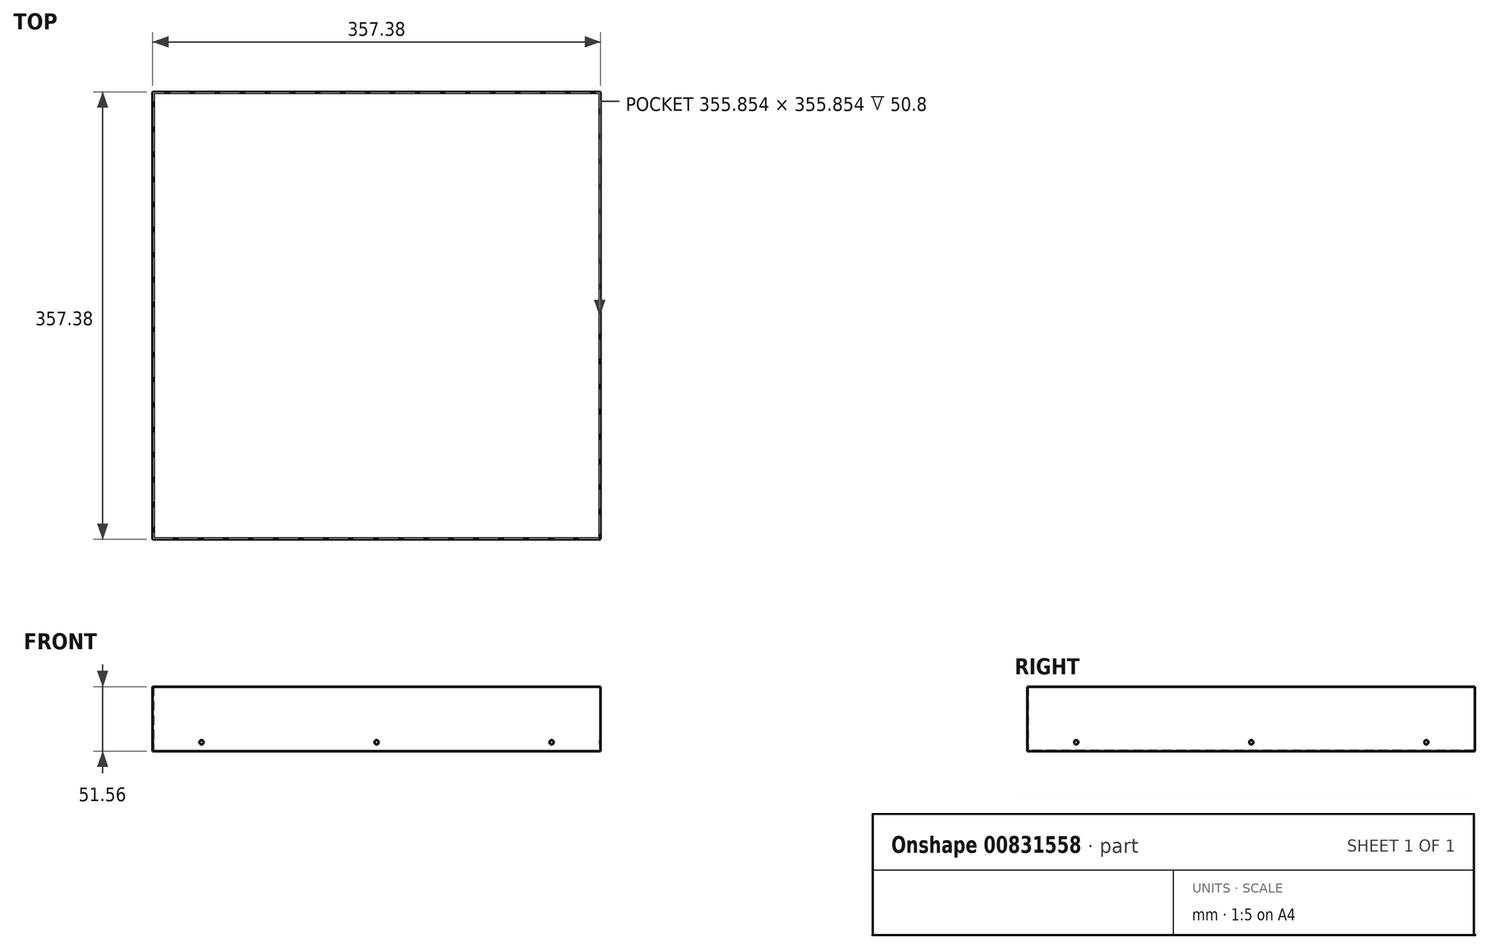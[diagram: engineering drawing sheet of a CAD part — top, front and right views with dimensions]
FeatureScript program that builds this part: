
annotation { "Feature Type Name" : "Feature", "Feature Type Description" : "" }
export const myFeature = defineFeature(function(context is Context, id is Id, definition is map)
    precondition{}
    {
        {
            var Q0;
            Q0=qCreatedBy(makeId("Top.planeOp"),FACE);
            var sketch = newSketch(context, id + "F0", { "sketchPlane" : qUnion([Q0])});
            skLineSegment(sketch, "E0.bottom", {"start": v(-178.69, 178.69) * mm, "end": v(178.69, 178.69) * mm});
            skLineSegment(sketch, "E0.top", {"start": v(-178.69, -178.69) * mm, "end": v(178.69, -178.69) * mm});
            skLineSegment(sketch, "E0.left", {"start": v(-178.69, 178.69) * mm, "end": v(-178.69, -178.69) * mm});
            skLineSegment(sketch, "E0.right", {"start": v(178.69, 178.69) * mm, "end": v(178.69, -178.69) * mm});
            skLineSegment(sketch, "E1", {"start": v(0, -178.69) * mm, "end": v(0, 0) * mm, "construction": true});
            skLineSegment(sketch, "E2", {"start": v(0, 0) * mm, "end": v(0, 178.69) * mm, "construction": true});
            skSolve(sketch);
        }
        {
            var Q0;
            Q0=qSketchRegion(id+"F0",true);
            extrude(context, id + "F1", {"entities" : qUnion([Q0]), "depth" : 51.56 * mm, "offsetDistance" : 25.4 * mm});
        }
        {
            var Q0;
            Q0=makeQuery(id+"F1.opExtrude","CAP_FACE",FACE,{"disambiguationData":[OSD([sQuery(id+"F0.wireOp",EDGE,"E0.bottom"),sQuery(id+"F0.wireOp",EDGE,"E0.top"),sQuery(id+"F0.wireOp",EDGE,"E0.left"),sQuery(id+"F0.wireOp",EDGE,"E0.right"),sQuery(id+"F0.wireOp",EDGE,"630c5ed9-5393-44ae-ab6d-eacaf67419a9.filletArc"),sQuery(id+"F0.wireOp",EDGE,"2e887e89-cee8-4952-a692-16c1ec2f9bde.filletArc"),sQuery(id+"F0.wireOp",EDGE,"c34aaee0-e8c7-4390-9170-ea4644db29ed.filletArc"),sQuery(id+"F0.wireOp",EDGE,"94ab99e3-fefe-4d1d-82de-1c0560d39820.filletArc")])],"isStart":false});
            shell(context, id + "F2", {"entities" : qUnion([Q0]), "thickness" : 0.76 * mm});
        }
        {
            var Q0;
            Q0=makeQuery(id+"F1.opExtrude","SWEPT_FACE",FACE,{"disambiguationData":[OSD([sQuery(id+"F0.wireOp",EDGE,"E0.top")])]});
            var sketch = newSketch(context, id + "F3", { "sketchPlane" : qUnion([Q0])});
            skPoint(sketch, "E3", {"position": v(-139.7, 7.11) * mm});
            skPoint(sketch, "E4", {"position": v(0, 7.11) * mm});
            skPoint(sketch, "E5", {"position": v(139.7, 7.11) * mm});
            skLineSegment(sketch, "E6", {"start": v(0, 0) * mm, "end": v(0, 7.11) * mm});
            skLineSegment(sketch, "E7", {"start": v(-139.7, 7.11) * mm, "end": v(0, 7.11) * mm});
            skLineSegment(sketch, "E8", {"start": v(139.7, 7.11) * mm, "end": v(0, 7.11) * mm});
            skSolve(sketch);
        }
        {
            var Q0;
            Q0=sQuery(id+"F3.wireOp",VERTEX,"E5");
            var Q1;
            Q1=sQuery(id+"F3.wireOp",VERTEX,"E4");
            var Q2;
            Q2=sQuery(id+"F3.wireOp",VERTEX,"E3");
            var Q3;
            Q3=makeQuery(id+"F1.opExtrude","SWEPT_BODY",BODY,{"disambiguationData":[OSD([sQuery(id+"F0.wireOp",EDGE,"E0.bottom"),sQuery(id+"F0.wireOp",EDGE,"E0.top"),sQuery(id+"F0.wireOp",EDGE,"E0.left"),sQuery(id+"F0.wireOp",EDGE,"E0.right"),sQuery(id+"F0.wireOp",EDGE,"630c5ed9-5393-44ae-ab6d-eacaf67419a9.filletArc"),sQuery(id+"F0.wireOp",EDGE,"2e887e89-cee8-4952-a692-16c1ec2f9bde.filletArc"),sQuery(id+"F0.wireOp",EDGE,"c34aaee0-e8c7-4390-9170-ea4644db29ed.filletArc"),sQuery(id+"F0.wireOp",EDGE,"94ab99e3-fefe-4d1d-82de-1c0560d39820.filletArc")])]});
            hole(context, id + "F4", {"style" : HoleStyle.SIMPLE, "endStyle" : HoleEndStyle.BLIND, "standardTappedOrClearance" : lookupTablePath({ "standard" : "ANSI", "size" : "#30 (0.13)", "type" : "Drilled" }), "standardBlindInLast" : lookupTablePath({ "standard" : "ANSI", "size" : "#30", "type" : "Drilled" }), "holeDiameter" : 3.26 * mm, "majorDiameter" : 6.35 * mm, "holeDepth" : 0.76 * mm, "isTappedThrough" : true, "tappedDepth" : 12.7 * mm, "tapClearance" : 3, "locations" : qUnion([Q0, Q1, Q2]), "scope" : qUnion([Q3])});
        }
        {
            var Q0;
            Q0=makeQuery(id+"F1.opExtrude","SWEPT_FACE",FACE,{"disambiguationData":[OSD([sQuery(id+"F0.wireOp",EDGE,"E0.left")])]});
            var sketch = newSketch(context, id + "F5", { "sketchPlane" : qUnion([Q0])});
            skPoint(sketch, "E9", {"position": v(-139.7, 7.11) * mm});
            skPoint(sketch, "E10", {"position": v(0, 7.11) * mm});
            skPoint(sketch, "E11", {"position": v(139.7, 7.11) * mm});
            skLineSegment(sketch, "E12", {"start": v(-139.7, 7.11) * mm, "end": v(0, 7.11) * mm});
            skLineSegment(sketch, "E13", {"start": v(0, 0) * mm, "end": v(0, 7.11) * mm});
            skLineSegment(sketch, "E14", {"start": v(0, 7.11) * mm, "end": v(139.7, 7.11) * mm});
            skSolve(sketch);
        }
        {
            var Q0;
            Q0=sQuery(id+"F5.wireOp",VERTEX,"E9");
            var Q1;
            Q1=sQuery(id+"F5.wireOp",VERTEX,"E10");
            var Q2;
            Q2=sQuery(id+"F5.wireOp",VERTEX,"E11");
            var Q3;
            Q3=makeQuery(id+"F1.opExtrude","SWEPT_BODY",BODY,{"disambiguationData":[OSD([sQuery(id+"F0.wireOp",EDGE,"E0.bottom"),sQuery(id+"F0.wireOp",EDGE,"E0.top"),sQuery(id+"F0.wireOp",EDGE,"E0.left"),sQuery(id+"F0.wireOp",EDGE,"E0.right"),sQuery(id+"F0.wireOp",EDGE,"630c5ed9-5393-44ae-ab6d-eacaf67419a9.filletArc"),sQuery(id+"F0.wireOp",EDGE,"2e887e89-cee8-4952-a692-16c1ec2f9bde.filletArc"),sQuery(id+"F0.wireOp",EDGE,"c34aaee0-e8c7-4390-9170-ea4644db29ed.filletArc"),sQuery(id+"F0.wireOp",EDGE,"94ab99e3-fefe-4d1d-82de-1c0560d39820.filletArc")])]});
            hole(context, id + "F6", {"style" : HoleStyle.SIMPLE, "endStyle" : HoleEndStyle.THROUGH, "standardTappedOrClearance" : lookupTablePath({ "standard" : "ANSI", "size" : "#30 (0.13)", "type" : "Drilled" }), "standardBlindInLast" : lookupTablePath({ "standard" : "ANSI", "size" : "#30", "type" : "Drilled" }), "holeDiameter" : 3.26 * mm, "majorDiameter" : 6.35 * mm, "isTappedThrough" : true, "tappedDepth" : 12.7 * mm, "tapClearance" : 3, "locations" : qUnion([Q0, Q1, Q2]), "scope" : qUnion([Q3])});
        }
    });
